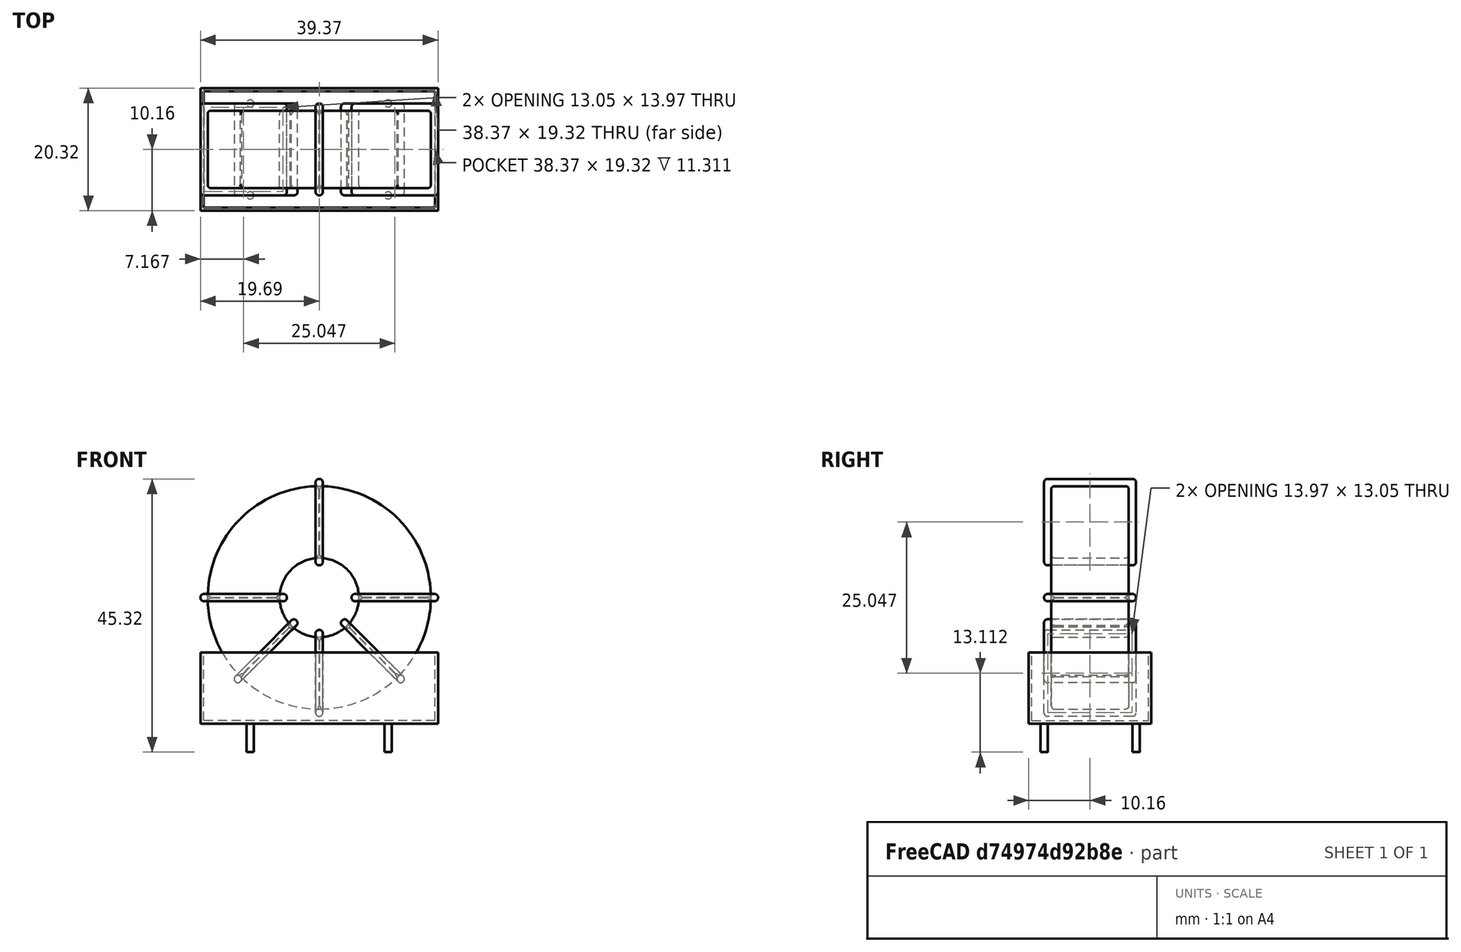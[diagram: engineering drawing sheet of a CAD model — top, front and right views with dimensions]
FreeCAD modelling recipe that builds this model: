
FCSTD DOCUMENT  (FreeCAD 0.16R6712 (Git))
Label: L_CommonMode_Toroid_Vertical_L39.4mm_W20.3mm_Px15.24mm_Py22.86mm_Bourns_8100
License: All rights reserved
LicenseURL: http://en.wikipedia.org/wiki/All_rights_reserved
objects: Sketcher::SketchObject×8, PartDesign::Pad×8, PartDesign::Fillet×5, Spreadsheet::Sheet×1, Part::MultiFuse×1
note: 30 computed .brp shape members not serialized (recipe doc carries the construction recipe); baked Part::Feature solids carry a one-line shape summary decoded from their .brp

FEATURE [Spreadsheet::Sheet] Spreadsheet  label="dimensions"
  cells = A1=Wx; B1(Wx)=39.37; C1(WW)=13.12333333333333; D1(iWx)=39.37; A2=Wy; B2(Wy)=15.24; D2(iWy)=20.32; A3=RM; B3(RMx)=15.24; C3(RMy)=22.86; A4=d_wire; B4(d_wire)=1.2; A5=H; B5(H)=31; A6=offsetx; B6(offsetx)=8.254999999999999
FEATURE [Sketcher::SketchObject] Sketch
  Placement = pos=(11.43,-7.62,0) rot=(1,0,0;1.5708rad)
  expr: Placement.Base.x = Spreadsheet.RMy / 2
  expr: Constraints[4] = Spreadsheet.WW / 2
  expr: Placement.Base.y = -Spreadsheet.RMx / 2
  expr: Constraints[0] = Spreadsheet.Wx / 2 - Spreadsheet.d_wire
  expr: Constraints[2] = Spreadsheet.Wx / 2 + Spreadsheet.d_wire + 0.5
  sketch-geometry (2):
    g0: Circle CenterX=0 CenterY=21.385 CenterZ=0 NormalX=0 NormalY=0 NormalZ=1 Radius=18.485
    g1: Circle CenterX=0 CenterY=21.385 CenterZ=0 NormalX=0 NormalY=0 NormalZ=1 Radius=6.56167
  constraints (5):
    c: Radius(g0) = 18.485
    c: DistanceX(g-1,g0) = 0
    c: DistanceY(g-1,g0) = 21.385
    c: Coincident(g1,g0)
    c: Radius(g1) = 6.56167
FEATURE [PartDesign::Pad] Pad
  Length = 12.84
  Length2 = 100
  Midplane = true
  Placement = pos=(11.43,-7.62,0) rot=(1,0,0;1.5708rad)
  Sketch = -> Sketch
  Type = 0
  expr: Length = Spreadsheet.Wy - 2 * Spreadsheet.d_wire
FEATURE [Sketcher::SketchObject] Sketch001
  Placement = pos=(0,0,0.75) rot=(0,0,1;0rad)
  expr: Constraints[4] = Spreadsheet.RMy
  expr: Constraints[2] = -Spreadsheet.RMx
  expr: Constraints[1] = Spreadsheet.d_wire / 2
  sketch-geometry (4):
    g0: Circle CenterX=0 CenterY=0 CenterZ=0 NormalX=0 NormalY=0 NormalZ=1 Radius=0.6
    g1: Circle CenterX=22.86 CenterY=-15.24 CenterZ=0 NormalX=0 NormalY=0 NormalZ=1 Radius=0.6
    g2: Circle CenterX=0 CenterY=-15.24 CenterZ=0 NormalX=0 NormalY=0 NormalZ=1 Radius=0.6
    g3: Circle CenterX=22.86 CenterY=0 CenterZ=0 NormalX=0 NormalY=0 NormalZ=1 Radius=0.6
  constraints (11):
    c: Equal(g0,g1)
    c: Radius(g0) = 0.6
    c: DistanceY(g-1,g1) = -15.24
    c: Coincident(g0,g-1)
    c: DistanceX(g-1,g1) = 22.86
    c: PointOnObject(g2,g-2)
    c: DistanceY(g-1,g3) = 0
    c: DistanceY(g2,g1) = 0
    c: DistanceX(g3,g1) = 0
    c: Equal(g3,g2)
    c: Equal(g2,g1)
FEATURE [PartDesign::Pad] Pad001
  Length = 5
  Length2 = 0
  Placement = pos=(0,0,0.75) rot=(0,0,1;0rad)
  Reversed = true
  Sketch = -> Sketch001
  Type = 0
FEATURE [PartDesign::Fillet] Fillet
  Base = -> Pad [Edge6,Edge3,Edge2]
  Placement = pos=(11.43,-7.62,0) rot=(1,0,0;1.5708rad)
  Radius = 0.5
FEATURE [Sketcher::SketchObject] Sketch003
  Placement = pos=(11.43,0,21.385) rot=(1,0,0;3.14159rad)
  expr: Placement.Base.x = Spreadsheet.RMy / 2
  expr: Constraints[18] = Spreadsheet.d_wire
  expr: Constraints[16] = Spreadsheet.d_wire
  expr: Constraints[19] = Spreadsheet.d_wire
  expr: Constraints[17] = Spreadsheet.d_wire
  expr: Placement.Base.y = -1 * (Spreadsheet.RMx - Spreadsheet.Wy) / 2
  expr: Constraints[21] = (Spreadsheet.Wx - Spreadsheet.WW) / 2 - Spreadsheet.d_wire
  expr: Constraints[22] = Spreadsheet.Wx / 2 - Spreadsheet.d_wire
  expr: Constraints[43] = Spreadsheet.d_wire
  expr: Constraints[48] = Spreadsheet.Wx - Spreadsheet.d_wire * 2
  expr: Constraints[49] = Spreadsheet.Wy
  expr: Placement.Base.z = Spreadsheet.Wx / 2 + Spreadsheet.d_wire + 0.5
  sketch-geometry (16):
    g0: LineSegment StartX=-5.36167 StartY=0 StartZ=0 EndX=-19.685 EndY=0 EndZ=0
    g1: LineSegment StartX=-19.685 StartY=0 StartZ=0 EndX=-19.685 EndY=15.24 EndZ=0
    g2: LineSegment StartX=-19.685 StartY=15.24 StartZ=0 EndX=-5.36167 EndY=15.24 EndZ=0
    g3: LineSegment StartX=-5.36167 StartY=15.24 StartZ=0 EndX=-5.36167 EndY=0 EndZ=0
    g4: LineSegment StartX=-18.485 StartY=14.04 StartZ=0 EndX=-6.56167 EndY=14.04 EndZ=0
    g5: LineSegment StartX=-6.56167 StartY=14.04 StartZ=0 EndX=-6.56167 EndY=1.2 EndZ=0
    g6: LineSegment StartX=-6.56167 StartY=1.2 StartZ=0 EndX=-18.485 EndY=1.2 EndZ=0
    g7: LineSegment StartX=-18.485 StartY=1.2 StartZ=0 EndX=-18.485 EndY=14.04 EndZ=0
    g8: LineSegment StartX=5.36167 StartY=15.24 StartZ=0 EndX=19.685 EndY=15.24 EndZ=0
    g9: LineSegment StartX=19.685 StartY=15.24 StartZ=0 EndX=19.685 EndY=0 EndZ=0
    g10: LineSegment StartX=19.685 StartY=0 StartZ=0 EndX=5.36167 EndY=0 EndZ=0
    g11: LineSegment StartX=5.36167 StartY=0 StartZ=0 EndX=5.36167 EndY=15.24 EndZ=0
    g12: LineSegment StartX=6.56167 StartY=14.04 StartZ=0 EndX=18.485 EndY=14.04 EndZ=0
    g13: LineSegment StartX=18.485 StartY=14.04 StartZ=0 EndX=18.485 EndY=1.2 EndZ=0
    g14: LineSegment StartX=18.485 StartY=1.2 StartZ=0 EndX=6.56167 EndY=1.2 EndZ=0
    g15: LineSegment StartX=6.56167 StartY=1.2 StartZ=0 EndX=6.56167 EndY=14.04 EndZ=0
  constraints (50):
    c: Horizontal(g0)
    c: Coincident(g1,g0)
    c: Vertical(g1)
    c: Coincident(g2,g1)
    c: Horizontal(g2)
    c: Coincident(g3,g2)
    c: Coincident(g3,g0)
    c: Vertical(g3)
    c: Coincident(g4,g5)
    c: Coincident(g5,g6)
    c: Coincident(g6,g7)
    c: Coincident(g7,g4)
    c: Horizontal(g4)
    c: Horizontal(g6)
    c: Vertical(g5)
    c: Vertical(g7)
    c: DistanceX(g1,g4) = 1.2
    c: DistanceY(g4,g1) = 1.2
    c: DistanceX(g5,g0) = 1.2
    c: DistanceY(g0,g5) = 1.2
    c: DistanceY(g-1,g0) = 0
    c: DistanceX(g6,g6) = 11.9233
    c: DistanceX(g6,g-1) = 18.485
    c: Coincident(g8,g9)
    c: Coincident(g9,g10)
    c: Coincident(g10,g11)
    c: Coincident(g11,g8)
    c: Horizontal(g8)
    c: Horizontal(g10)
    c: Vertical(g9)
    c: Vertical(g11)
    c: Coincident(g12,g13)
    c: Coincident(g13,g14)
    c: Coincident(g14,g15)
    c: Coincident(g15,g12)
    c: Horizontal(g12)
    c: Horizontal(g14)
    c: Vertical(g13)
    c: Vertical(g15)
    c: DistanceY(g8,g2) = 0
    c: DistanceY(g10,g0) = 0
    c: DistanceY(g14,g5) = 0
    c: DistanceY(g12,g4) = 0
    c: DistanceX(g8,g12) = 1.2
    c: Equal(g8,g2)
    c: Equal(g12,g4)
    c: Equal(g9,g1)
    c: Equal(g13,g7)
    c: DistanceX(g4,g12) = 36.97
    c: DistanceY(g0,g1) = 15.24
FEATURE [PartDesign::Pad] Pad002
  Length = 1.2
  Length2 = 100
  Midplane = true
  Placement = pos=(11.43,0,21.385) rot=(1,0,0;3.14159rad)
  Sketch = -> Sketch003
  Type = 0
  expr: Length = Spreadsheet.d_wire
FEATURE [PartDesign::Fillet] Fillet001
  Base = -> Pad002 [Edge38,Edge41,Edge42,Edge43,Edge29,Edge32,Edge33,Edge34,Edge25,Edge35,Edge36,Edge13,Edge14,Edge15,Edge16,Edge17,Edge18,Edge19,Edge1,Edge2,Edge3,Edge4,Edge5,Edge6,Edge7,Edge37,Edge39,Edge40,Edge20,Edge23,Edge24,Edge21,Edge22,Edge8,Edge9,Edge10,Edge11,Edge12,Edge26,Edge27,+8 more]
  Placement = pos=(11.43,0,21.385) rot=(1,0,0;3.14159rad)
  Radius = 0.564
  expr: Radius = Spreadsheet.d_wire * 0.47
FEATURE [Sketcher::SketchObject] Sketch004
  Placement = pos=(11.43,0,21.385) rot=(0.92388,0,0.382683;3.14159rad)
  expr: Placement.Base.x = Spreadsheet.RMy / 2
  expr: Constraints[18] = Spreadsheet.d_wire
  expr: Constraints[16] = Spreadsheet.d_wire
  expr: Constraints[19] = Spreadsheet.d_wire
  expr: Constraints[17] = Spreadsheet.d_wire
  expr: Placement.Base.y = -1 * (Spreadsheet.RMx - Spreadsheet.Wy) / 2
  expr: Constraints[21] = (Spreadsheet.Wx - Spreadsheet.WW) / 2 - Spreadsheet.d_wire
  expr: Constraints[22] = Spreadsheet.Wx / 2 - Spreadsheet.d_wire
  expr: Constraints[43] = Spreadsheet.d_wire
  expr: Constraints[48] = Spreadsheet.Wx - 2 * Spreadsheet.d_wire
  expr: Constraints[49] = Spreadsheet.Wy
  expr: Placement.Base.z = Spreadsheet.Wx / 2 + Spreadsheet.d_wire + 0.5
  sketch-geometry (16):
    g0: LineSegment StartX=-5.36167 StartY=0 StartZ=0 EndX=-19.685 EndY=0 EndZ=0
    g1: LineSegment StartX=-19.685 StartY=0 StartZ=0 EndX=-19.685 EndY=15.24 EndZ=0
    g2: LineSegment StartX=-19.685 StartY=15.24 StartZ=0 EndX=-5.36167 EndY=15.24 EndZ=0
    g3: LineSegment StartX=-5.36167 StartY=15.24 StartZ=0 EndX=-5.36167 EndY=0 EndZ=0
    g4: LineSegment StartX=-18.485 StartY=14.04 StartZ=0 EndX=-6.56167 EndY=14.04 EndZ=0
    g5: LineSegment StartX=-6.56167 StartY=14.04 StartZ=0 EndX=-6.56167 EndY=1.2 EndZ=0
    g6: LineSegment StartX=-6.56167 StartY=1.2 StartZ=0 EndX=-18.485 EndY=1.2 EndZ=0
    g7: LineSegment StartX=-18.485 StartY=1.2 StartZ=0 EndX=-18.485 EndY=14.04 EndZ=0
    g8: LineSegment StartX=5.36167 StartY=15.24 StartZ=0 EndX=19.685 EndY=15.24 EndZ=0
    g9: LineSegment StartX=19.685 StartY=15.24 StartZ=0 EndX=19.685 EndY=0 EndZ=0
    g10: LineSegment StartX=19.685 StartY=0 StartZ=0 EndX=5.36167 EndY=0 EndZ=0
    g11: LineSegment StartX=5.36167 StartY=0 StartZ=0 EndX=5.36167 EndY=15.24 EndZ=0
    g12: LineSegment StartX=6.56167 StartY=14.04 StartZ=0 EndX=18.485 EndY=14.04 EndZ=0
    g13: LineSegment StartX=18.485 StartY=14.04 StartZ=0 EndX=18.485 EndY=1.2 EndZ=0
    g14: LineSegment StartX=18.485 StartY=1.2 StartZ=0 EndX=6.56167 EndY=1.2 EndZ=0
    g15: LineSegment StartX=6.56167 StartY=1.2 StartZ=0 EndX=6.56167 EndY=14.04 EndZ=0
  constraints (50):
    c: Horizontal(g0)
    c: Coincident(g1,g0)
    c: Vertical(g1)
    c: Coincident(g2,g1)
    c: Horizontal(g2)
    c: Coincident(g3,g2)
    c: Coincident(g3,g0)
    c: Vertical(g3)
    c: Coincident(g4,g5)
    c: Coincident(g5,g6)
    c: Coincident(g6,g7)
    c: Coincident(g7,g4)
    c: Horizontal(g4)
    c: Horizontal(g6)
    c: Vertical(g5)
    c: Vertical(g7)
    c: DistanceX(g1,g4) = 1.2
    c: DistanceY(g4,g1) = 1.2
    c: DistanceX(g5,g0) = 1.2
    c: DistanceY(g0,g5) = 1.2
    c: DistanceY(g-1,g0) = 0
    c: DistanceX(g6,g6) = 11.9233
    c: DistanceX(g6,g-1) = 18.485
    c: Coincident(g8,g9)
    c: Coincident(g9,g10)
    c: Coincident(g10,g11)
    c: Coincident(g11,g8)
    c: Horizontal(g8)
    c: Horizontal(g10)
    c: Vertical(g9)
    c: Vertical(g11)
    c: Coincident(g12,g13)
    c: Coincident(g13,g14)
    c: Coincident(g14,g15)
    c: Coincident(g15,g12)
    c: Horizontal(g12)
    c: Horizontal(g14)
    c: Vertical(g13)
    c: Vertical(g15)
    c: DistanceY(g8,g2) = 0
    c: DistanceY(g10,g0) = 0
    c: DistanceY(g14,g5) = 0
    c: DistanceY(g12,g4) = 0
    c: DistanceX(g8,g12) = 1.2
    c: Equal(g8,g2)
    c: Equal(g12,g4)
    c: Equal(g9,g1)
    c: Equal(g13,g7)
    c: DistanceX(g4,g12) = 36.97
    c: DistanceY(g0,g1) = 15.24
FEATURE [PartDesign::Pad] Pad003
  Length = 1.2
  Length2 = 100
  Midplane = true
  Placement = pos=(11.43,0,21.385) rot=(0.92388,0,0.382683;3.14159rad)
  Sketch = -> Sketch004
  Type = 0
  expr: Length = Spreadsheet.d_wire
FEATURE [PartDesign::Fillet] Fillet002
  Base = -> Pad003 [Edge38,Edge41,Edge42,Edge43,Edge29,Edge32,Edge33,Edge34,Edge25,Edge35,Edge36,Edge13,Edge14,Edge15,Edge16,Edge17,Edge18,Edge19,Edge1,Edge2,Edge3,Edge4,Edge5,Edge6,Edge7,Edge37,Edge39,Edge40,Edge20,Edge23,Edge24,Edge21,Edge22,Edge8,Edge9,Edge10,Edge11,Edge12,Edge26,Edge27,+8 more]
  Placement = pos=(11.43,0,21.385) rot=(0.92388,0,0.382683;3.14159rad)
  Radius = 0.564
  expr: Radius = Spreadsheet.d_wire * 0.47
FEATURE [Sketcher::SketchObject] Sketch005
  Placement = pos=(11.43,0,21.385) rot=(0.92388,0,-0.382683;3.14159rad)
  expr: Placement.Base.x = Spreadsheet.RMy / 2
  expr: Constraints[18] = Spreadsheet.d_wire
  expr: Constraints[16] = Spreadsheet.d_wire
  expr: Constraints[19] = Spreadsheet.d_wire
  expr: Constraints[17] = Spreadsheet.d_wire
  expr: Placement.Base.y = -1 * (Spreadsheet.RMx - Spreadsheet.Wy) / 2
  expr: Constraints[21] = (Spreadsheet.Wx - Spreadsheet.WW) / 2 - Spreadsheet.d_wire
  expr: Constraints[22] = Spreadsheet.Wx / 2 - Spreadsheet.d_wire
  expr: Constraints[43] = Spreadsheet.d_wire
  expr: Constraints[48] = Spreadsheet.Wx - 2 * Spreadsheet.d_wire
  expr: Constraints[49] = Spreadsheet.Wy
  expr: Placement.Base.z = Spreadsheet.Wx / 2 + Spreadsheet.d_wire + 0.5
  sketch-geometry (16):
    g0: LineSegment StartX=-5.36167 StartY=0 StartZ=0 EndX=-19.685 EndY=0 EndZ=0
    g1: LineSegment StartX=-19.685 StartY=0 StartZ=0 EndX=-19.685 EndY=15.24 EndZ=0
    g2: LineSegment StartX=-19.685 StartY=15.24 StartZ=0 EndX=-5.36167 EndY=15.24 EndZ=0
    g3: LineSegment StartX=-5.36167 StartY=15.24 StartZ=0 EndX=-5.36167 EndY=0 EndZ=0
    g4: LineSegment StartX=-18.485 StartY=14.04 StartZ=0 EndX=-6.56167 EndY=14.04 EndZ=0
    g5: LineSegment StartX=-6.56167 StartY=14.04 StartZ=0 EndX=-6.56167 EndY=1.2 EndZ=0
    g6: LineSegment StartX=-6.56167 StartY=1.2 StartZ=0 EndX=-18.485 EndY=1.2 EndZ=0
    g7: LineSegment StartX=-18.485 StartY=1.2 StartZ=0 EndX=-18.485 EndY=14.04 EndZ=0
    g8: LineSegment StartX=5.36167 StartY=15.24 StartZ=0 EndX=19.685 EndY=15.24 EndZ=0
    g9: LineSegment StartX=19.685 StartY=15.24 StartZ=0 EndX=19.685 EndY=0 EndZ=0
    g10: LineSegment StartX=19.685 StartY=0 StartZ=0 EndX=5.36167 EndY=0 EndZ=0
    g11: LineSegment StartX=5.36167 StartY=0 StartZ=0 EndX=5.36167 EndY=15.24 EndZ=0
    g12: LineSegment StartX=6.56167 StartY=14.04 StartZ=0 EndX=18.485 EndY=14.04 EndZ=0
    g13: LineSegment StartX=18.485 StartY=14.04 StartZ=0 EndX=18.485 EndY=1.2 EndZ=0
    g14: LineSegment StartX=18.485 StartY=1.2 StartZ=0 EndX=6.56167 EndY=1.2 EndZ=0
    g15: LineSegment StartX=6.56167 StartY=1.2 StartZ=0 EndX=6.56167 EndY=14.04 EndZ=0
  constraints (50):
    c: Horizontal(g0)
    c: Coincident(g1,g0)
    c: Vertical(g1)
    c: Coincident(g2,g1)
    c: Horizontal(g2)
    c: Coincident(g3,g2)
    c: Coincident(g3,g0)
    c: Vertical(g3)
    c: Coincident(g4,g5)
    c: Coincident(g5,g6)
    c: Coincident(g6,g7)
    c: Coincident(g7,g4)
    c: Horizontal(g4)
    c: Horizontal(g6)
    c: Vertical(g5)
    c: Vertical(g7)
    c: DistanceX(g1,g4) = 1.2
    c: DistanceY(g4,g1) = 1.2
    c: DistanceX(g5,g0) = 1.2
    c: DistanceY(g0,g5) = 1.2
    c: DistanceY(g-1,g0) = 0
    c: DistanceX(g6,g6) = 11.9233
    c: DistanceX(g6,g-1) = 18.485
    c: Coincident(g8,g9)
    c: Coincident(g9,g10)
    c: Coincident(g10,g11)
    c: Coincident(g11,g8)
    c: Horizontal(g8)
    c: Horizontal(g10)
    c: Vertical(g9)
    c: Vertical(g11)
    c: Coincident(g12,g13)
    c: Coincident(g13,g14)
    c: Coincident(g14,g15)
    c: Coincident(g15,g12)
    c: Horizontal(g12)
    c: Horizontal(g14)
    c: Vertical(g13)
    c: Vertical(g15)
    c: DistanceY(g8,g2) = 0
    c: DistanceY(g10,g0) = 0
    c: DistanceY(g14,g5) = 0
    c: DistanceY(g12,g4) = 0
    c: DistanceX(g8,g12) = 1.2
    c: Equal(g8,g2)
    c: Equal(g12,g4)
    c: Equal(g9,g1)
    c: Equal(g13,g7)
    c: DistanceX(g4,g12) = 36.97
    c: DistanceY(g0,g1) = 15.24
FEATURE [PartDesign::Pad] Pad004
  Length = 1.2
  Length2 = 100
  Midplane = true
  Placement = pos=(11.43,0,21.385) rot=(0.92388,0,-0.382683;3.14159rad)
  Sketch = -> Sketch005
  Type = 0
  expr: Length = Spreadsheet.d_wire
FEATURE [PartDesign::Fillet] Fillet003
  Base = -> Pad004 [Edge38,Edge41,Edge42,Edge43,Edge29,Edge32,Edge33,Edge34,Edge25,Edge35,Edge36,Edge13,Edge14,Edge15,Edge16,Edge17,Edge18,Edge19,Edge1,Edge2,Edge3,Edge4,Edge5,Edge6,Edge7,Edge37,Edge39,Edge40,Edge20,Edge23,Edge24,Edge21,Edge22,Edge8,Edge9,Edge10,Edge11,Edge12,Edge26,Edge27,+8 more]
  Placement = pos=(11.43,0,21.385) rot=(0.92388,0,-0.382683;3.14159rad)
  Radius = 0.564
  expr: Radius = Spreadsheet.d_wire * 0.47
FEATURE [Sketcher::SketchObject] Sketch006
  Placement = pos=(11.43,0,21.385) rot=(0.707107,0,0.707107;3.14159rad)
  expr: Placement.Base.x = Spreadsheet.RMy / 2
  expr: Constraints[18] = Spreadsheet.d_wire
  expr: Constraints[16] = Spreadsheet.d_wire
  expr: Constraints[19] = Spreadsheet.d_wire
  expr: Constraints[17] = Spreadsheet.d_wire
  expr: Placement.Base.y = -1 * (Spreadsheet.RMx - Spreadsheet.Wy) / 2
  expr: Constraints[21] = (Spreadsheet.Wx - Spreadsheet.WW) / 2 - Spreadsheet.d_wire
  expr: Constraints[22] = Spreadsheet.Wx / 2 - Spreadsheet.d_wire
  expr: Constraints[43] = Spreadsheet.d_wire
  expr: Constraints[48] = Spreadsheet.Wx - Spreadsheet.d_wire * 2
  expr: Constraints[49] = Spreadsheet.Wy
  expr: Placement.Base.z = Spreadsheet.Wx / 2 + Spreadsheet.d_wire + 0.5
  sketch-geometry (16):
    g0: LineSegment StartX=-5.36167 StartY=0 StartZ=0 EndX=-19.685 EndY=0 EndZ=0
    g1: LineSegment StartX=-19.685 StartY=0 StartZ=0 EndX=-19.685 EndY=15.24 EndZ=0
    g2: LineSegment StartX=-19.685 StartY=15.24 StartZ=0 EndX=-5.36167 EndY=15.24 EndZ=0
    g3: LineSegment StartX=-5.36167 StartY=15.24 StartZ=0 EndX=-5.36167 EndY=0 EndZ=0
    g4: LineSegment StartX=-18.485 StartY=14.04 StartZ=0 EndX=-6.56167 EndY=14.04 EndZ=0
    g5: LineSegment StartX=-6.56167 StartY=14.04 StartZ=0 EndX=-6.56167 EndY=1.2 EndZ=0
    g6: LineSegment StartX=-6.56167 StartY=1.2 StartZ=0 EndX=-18.485 EndY=1.2 EndZ=0
    g7: LineSegment StartX=-18.485 StartY=1.2 StartZ=0 EndX=-18.485 EndY=14.04 EndZ=0
    g8: LineSegment StartX=5.36167 StartY=15.24 StartZ=0 EndX=19.685 EndY=15.24 EndZ=0
    g9: LineSegment StartX=19.685 StartY=15.24 StartZ=0 EndX=19.685 EndY=0 EndZ=0
    g10: LineSegment StartX=19.685 StartY=0 StartZ=0 EndX=5.36167 EndY=0 EndZ=0
    g11: LineSegment StartX=5.36167 StartY=0 StartZ=0 EndX=5.36167 EndY=15.24 EndZ=0
    g12: LineSegment StartX=6.56167 StartY=14.04 StartZ=0 EndX=18.485 EndY=14.04 EndZ=0
    g13: LineSegment StartX=18.485 StartY=14.04 StartZ=0 EndX=18.485 EndY=1.2 EndZ=0
    g14: LineSegment StartX=18.485 StartY=1.2 StartZ=0 EndX=6.56167 EndY=1.2 EndZ=0
    g15: LineSegment StartX=6.56167 StartY=1.2 StartZ=0 EndX=6.56167 EndY=14.04 EndZ=0
  constraints (50):
    c: Horizontal(g0)
    c: Coincident(g1,g0)
    c: Vertical(g1)
    c: Coincident(g2,g1)
    c: Horizontal(g2)
    c: Coincident(g3,g2)
    c: Coincident(g3,g0)
    c: Vertical(g3)
    c: Coincident(g4,g5)
    c: Coincident(g5,g6)
    c: Coincident(g6,g7)
    c: Coincident(g7,g4)
    c: Horizontal(g4)
    c: Horizontal(g6)
    c: Vertical(g5)
    c: Vertical(g7)
    c: DistanceX(g1,g4) = 1.2
    c: DistanceY(g4,g1) = 1.2
    c: DistanceX(g5,g0) = 1.2
    c: DistanceY(g0,g5) = 1.2
    c: DistanceY(g-1,g0) = 0
    c: DistanceX(g6,g6) = 11.9233
    c: DistanceX(g6,g-1) = 18.485
    c: Coincident(g8,g9)
    c: Coincident(g9,g10)
    c: Coincident(g10,g11)
    c: Coincident(g11,g8)
    c: Horizontal(g8)
    c: Horizontal(g10)
    c: Vertical(g9)
    c: Vertical(g11)
    c: Coincident(g12,g13)
    c: Coincident(g13,g14)
    c: Coincident(g14,g15)
    c: Coincident(g15,g12)
    c: Horizontal(g12)
    c: Horizontal(g14)
    c: Vertical(g13)
    c: Vertical(g15)
    c: DistanceY(g8,g2) = 0
    c: DistanceY(g10,g0) = 0
    c: DistanceY(g14,g5) = 0
    c: DistanceY(g12,g4) = 0
    c: DistanceX(g8,g12) = 1.2
    c: Equal(g8,g2)
    c: Equal(g12,g4)
    c: Equal(g9,g1)
    c: Equal(g13,g7)
    c: DistanceX(g4,g12) = 36.97
    c: DistanceY(g0,g1) = 15.24
FEATURE [PartDesign::Pad] Pad005
  Length = 1.2
  Length2 = 100
  Midplane = true
  Placement = pos=(11.43,0,21.385) rot=(0.707107,0,0.707107;3.14159rad)
  Sketch = -> Sketch006
  Type = 0
  expr: Length = Spreadsheet.d_wire
FEATURE [PartDesign::Fillet] Fillet004
  Base = -> Pad005 [Edge38,Edge41,Edge42,Edge43,Edge29,Edge32,Edge33,Edge34,Edge25,Edge35,Edge36,Edge13,Edge14,Edge15,Edge16,Edge17,Edge18,Edge19,Edge1,Edge2,Edge3,Edge4,Edge5,Edge6,Edge7,Edge37,Edge39,Edge40,Edge20,Edge23,Edge24,Edge21,Edge22,Edge8,Edge9,Edge10,Edge11,Edge12,Edge26,Edge27,+8 more]
  Placement = pos=(11.43,0,21.385) rot=(0.707107,0,0.707107;3.14159rad)
  Radius = 0.564
  expr: Radius = Spreadsheet.d_wire * 0.47
FEATURE [Sketcher::SketchObject] Sketch007
  Placement = pos=(11.43,0,0.5) rot=(0,0,1;0rad)
  expr: Placement.Base.x = Spreadsheet.RMy / 2
  expr: Placement.Base.z = 0.5
  expr: Constraints[11] = Spreadsheet.iWx / 2
  expr: Constraints[10] = (Spreadsheet.iWy - Spreadsheet.RMx) / 2
  expr: Constraints[9] = Spreadsheet.iWy
  expr: Constraints[8] = Spreadsheet.iWx
  sketch-geometry (4):
    g0: LineSegment StartX=-19.685 StartY=2.54 StartZ=0 EndX=19.685 EndY=2.54 EndZ=0
    g1: LineSegment StartX=19.685 StartY=2.54 StartZ=0 EndX=19.685 EndY=-17.78 EndZ=0
    g2: LineSegment StartX=19.685 StartY=-17.78 StartZ=0 EndX=-19.685 EndY=-17.78 EndZ=0
    g3: LineSegment StartX=-19.685 StartY=-17.78 StartZ=0 EndX=-19.685 EndY=2.54 EndZ=0
  constraints (12):
    c: Coincident(g0,g1)
    c: Coincident(g1,g2)
    c: Coincident(g2,g3)
    c: Coincident(g3,g0)
    c: Horizontal(g0)
    c: Horizontal(g2)
    c: Vertical(g1)
    c: Vertical(g3)
    c: DistanceX(g0,g0) = 39.37
    c: DistanceY(g3,g3) = 20.32
    c: DistanceY(g-1,g0) = 2.54
    c: DistanceX(g0,g-1) = 19.685
FEATURE [PartDesign::Pad] Pad006
  Length = 0.5
  Length2 = 100
  Placement = pos=(11.43,0,0.5) rot=(0,0,1;0rad)
  Sketch = -> Sketch007
  Type = 0
FEATURE [Sketcher::SketchObject] Sketch008
  Placement = pos=(11.43,0,0.5) rot=(0,0,1;0rad)
  expr: Placement.Base.x = Spreadsheet.RMy / 2
  expr: Constraints[8] = Spreadsheet.iWx
  expr: Constraints[9] = Spreadsheet.iWy
  expr: Constraints[10] = (Spreadsheet.iWy - Spreadsheet.RMx) / 2
  expr: Placement.Base.z = 0.5
  expr: Constraints[21] = 0.5
  expr: Constraints[11] = Spreadsheet.iWx / 2
  sketch-geometry (8):
    g0: LineSegment StartX=-19.685 StartY=2.54 StartZ=0 EndX=19.685 EndY=2.54 EndZ=0
    g1: LineSegment StartX=19.685 StartY=2.54 StartZ=0 EndX=19.685 EndY=-17.78 EndZ=0
    g2: LineSegment StartX=19.685 StartY=-17.78 StartZ=0 EndX=-19.685 EndY=-17.78 EndZ=0
    g3: LineSegment StartX=-19.685 StartY=-17.78 StartZ=0 EndX=-19.685 EndY=2.54 EndZ=0
    g4: LineSegment StartX=-19.185 StartY=2.04 StartZ=0 EndX=19.185 EndY=2.04 EndZ=0
    g5: LineSegment StartX=19.185 StartY=2.04 StartZ=0 EndX=19.185 EndY=-17.28 EndZ=0
    g6: LineSegment StartX=19.185 StartY=-17.28 StartZ=0 EndX=-19.185 EndY=-17.28 EndZ=0
    g7: LineSegment StartX=-19.185 StartY=-17.28 StartZ=0 EndX=-19.185 EndY=2.04 EndZ=0
  constraints (24):
    c: Coincident(g0,g1)
    c: Coincident(g1,g2)
    c: Coincident(g2,g3)
    c: Coincident(g3,g0)
    c: Horizontal(g0)
    c: Horizontal(g2)
    c: Vertical(g1)
    c: Vertical(g3)
    c: DistanceX(g0,g0) = 39.37
    c: DistanceY(g3,g3) = 20.32
    c: DistanceY(g-1,g0) = 2.54
    c: DistanceX(g0,g-1) = 19.685
    c: Coincident(g4,g5)
    c: Coincident(g5,g6)
    c: Coincident(g6,g7)
    c: Coincident(g7,g4)
    c: Horizontal(g4)
    c: Horizontal(g6)
    c: Vertical(g5)
    c: Vertical(g7)
    c: DistanceX(g5,g1) = 0.5
    c: DistanceY(g1,g5) = 0.5
    c: DistanceX(g0,g4) = 0.5
    c: DistanceY(g4,g0) = 0.5
FEATURE [PartDesign::Pad] Pad007
  Length = 11.811
  Length2 = 100
  Placement = pos=(11.43,0,0.5) rot=(0,0,1;0rad)
  Sketch = -> Sketch008
  Type = 0
  expr: Length = Spreadsheet.Wx * 0.3
FEATURE [Part::MultiFuse] Pad001_mp_cp  label="L_CommonMode_Toroid_Vertical_L39.4mm_W20.3mm_Px15.24mm_Py22.86mm_Bourns_8100"
  Shapes = -> [Pad001,Fillet,Fillet001,Fillet002,Fillet003,Fillet004,Pad006,Pad007]
